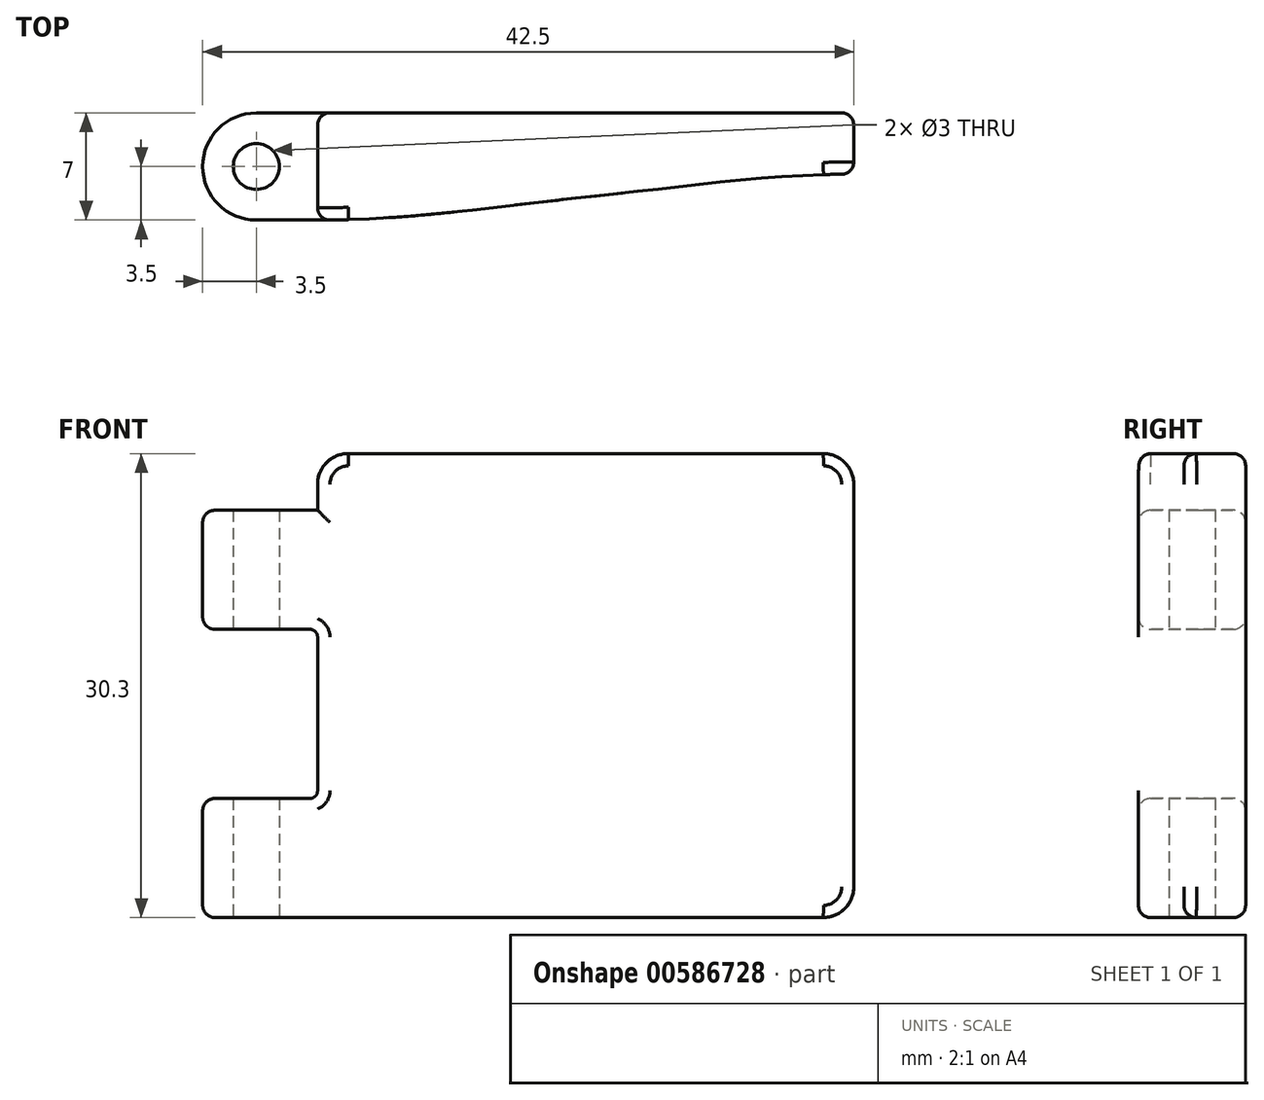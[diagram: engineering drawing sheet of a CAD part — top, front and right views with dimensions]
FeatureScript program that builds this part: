
annotation { "Feature Type Name" : "Feature", "Feature Type Description" : "" }
export const myFeature = defineFeature(function(context is Context, id is Id, definition is map)
    precondition{}
    {
        {
            var Q0;
            Q0=qCreatedBy(makeId("Top.planeOp"),FACE);
            var sketch = newSketch(context, id + "F0", { "sketchPlane" : qUnion([Q0])});
            skCircle(sketch, "E0", {"center": v(-4, -3.5) * mm, "radius": 3.5 * mm, "construction": true});
            skCircle(sketch, "E1", {"center": v(-4, -3.5) * mm, "radius": 1.5 * mm});
            skLineSegment(sketch, "E2", {"start": v(-4, -7) * mm, "end": v(0, -7) * mm});
            skLineSegment(sketch, "E3", {"start": v(-4, 0) * mm, "end": v(0, 0) * mm});
            skArc(sketch, "E4", {"start": v(-4, 0) * mm, "mid": v(-7.5, -3.5) * mm, "end": v(-4, -7) * mm});
            skLineSegment(sketch, "E5", {"start": v(0, -7) * mm, "end": v(0, 0) * mm});
            skSolve(sketch);
        }
        {
            var Q0;
            Q0 = qSketchRegion(id + "F0", true);
            extrude(context, id + "F1", {"entities" : qUnion([Q0]), "endBound" : BoundingType.SYMMETRIC, "depth" : 26.6 * mm, "offsetDistance" : 25 * mm});
        }
        {
            var Q0;
            Q0=qCreatedBy(makeId("Top.planeOp"),FACE);
            var sketch = newSketch(context, id + "F2", { "sketchPlane" : qUnion([Q0])});
            skLineSegment(sketch, "E6", {"start": v(0, 0) * mm, "end": v(35, 0) * mm});
            skLineSegment(sketch, "E7", {"start": v(35, 0) * mm, "end": v(35, -4) * mm});
            skFitSpline(sketch, "E8", {"points": [v(35, -4) * mm, v(22, -5) * mm, v(13, -6) * mm, v(0, -7) * mm], "startDerivative": vector(-42.5, 0) * mm, "endDerivative": vector(-42.5, 0) * mm});
            skLineSegment(sketch, "E9", {"start": v(0, 0) * mm, "end": v(0, -7) * mm});
            skSolve(sketch);
        }
        {
            var Q0;
            Q0=makeQuery(id+"F2.imprint","IMPRINT",FACE,{"disambiguationData":[TD([[makeQuery(id+"F2.imprint","IMPRINT",EDGE,{"derivedFrom":sQuery(id+"F2.wireOp",EDGE,"E6")}),-1.0]])]});
            var Q1;
            Q1=makeQuery(id+"F1.opExtrude","CAP_FACE",FACE,{"disambiguationData":[OSD([sQuery(id+"F0.wireOp",EDGE,"E1"),sQuery(id+"F0.wireOp",EDGE,"E2"),sQuery(id+"F0.wireOp",EDGE,"E3"),sQuery(id+"F0.wireOp",EDGE,"E4"),sQuery(id+"F0.wireOp",EDGE,"E5")])],"isStart":true});
            extrude(context, id + "F3", {"entities" : qUnion([Q0]), "operationType" : NewBodyOperationType.ADD, "depth" : 17 * mm, "offsetDistance" : 25 * mm, "hasSecondDirection" : true, "secondDirectionBound" : SecondDirectionBoundingType.UP_TO_SURFACE, "secondDirectionOppositeDirection" : true, "secondDirectionDepth" : 25 * mm, "secondDirectionBoundEntityFace" : qUnion([Q1])});
        }
        {
            var Q0;
            Q0 = qSketchRegion(id + "F0", true);
            extrude(context, id + "F4", {"entities" : qUnion([Q0]), "operationType" : NewBodyOperationType.REMOVE, "endBound" : BoundingType.SYMMETRIC, "depth" : 11.05 * mm, "offsetDistance" : 25 * mm});
        }
        {
            var Q0;
            Q0=makeQuery(id+"F1.opExtrude","CAP_EDGE",EDGE,{"disambiguationData":[OSD([sQuery(id+"F0.wireOp",EDGE,"E5")])],"isStart":false});
            var Q1;
            Q1=makeQuery(id+"F4.boolean.opBoolean","COPY",EDGE,{"derivedFrom":makeQuery(id+"F4.opExtrude","CAP_EDGE",EDGE,{"disambiguationData":[OSD([sQuery(id+"F0.wireOp",EDGE,"E5")])],"isStart":false})});
            var Q2;
            Q2=makeQuery(id+"F4.boolean.opBoolean","COPY",EDGE,{"derivedFrom":makeQuery(id+"F4.opExtrude","CAP_EDGE",EDGE,{"disambiguationData":[OSD([sQuery(id+"F0.wireOp",EDGE,"E5")])],"isStart":true})});
            fillet(context, id + "F5", {"entities" : qUnion([Q0, Q1, Q2]), "radius" : 0.5 * mm, "tangentPropagation" : true, "allowEdgeOverflow" : false});
        }
        {
            var Q0;
            Q0=makeQuery(id+"F3.opExtrude","CAP_EDGE",EDGE,{"disambiguationData":[OSD([sQuery(id+"F2.wireOp",EDGE,"E9")])],"isStart":false});
            var Q1;
            Q1=makeQuery(id+"F3.opExtrude","CAP_EDGE",EDGE,{"disambiguationData":[OSD([sQuery(id+"F2.wireOp",EDGE,"E7")])],"isStart":false});
            var Q2;
            Q2=makeQuery(id+"F3.opExtrude","CAP_EDGE",EDGE,{"disambiguationData":[OSD([sQuery(id+"F2.wireOp",EDGE,"E7")])],"isStart":true});
            fillet(context, id + "F6", {"entities" : qUnion([Q0, Q1, Q2]), "radius" : 2 * mm, "tangentPropagation" : true, "allowEdgeOverflow" : false});
        }
        {
            var Q0;
            Q0=makeQuery(id+"F3.opExtrude","SWEPT_FACE",FACE,{"disambiguationData":[OSD([sQuery(id+"F2.wireOp",EDGE,"E8")])]});
            var Q1;
            Q1=makeQuery(id+"F3.boolean.opBoolean","MERGE",FACE,{"derivedFrom":[makeQuery(id+"F1.opExtrude","SWEPT_FACE",FACE,{"disambiguationData":[OSD([sQuery(id+"F0.wireOp",EDGE,"E3")])]}),makeQuery(id+"F3.opExtrude","SWEPT_FACE",FACE,{"disambiguationData":[OSD([sQuery(id+"F2.wireOp",EDGE,"E6")])]})]});
            fillet(context, id + "F7", {"entities" : qUnion([Q0, Q1]), "radius" : 0.8 * mm, "tangentPropagation" : true, "allowEdgeOverflow" : false});
        }
    });
